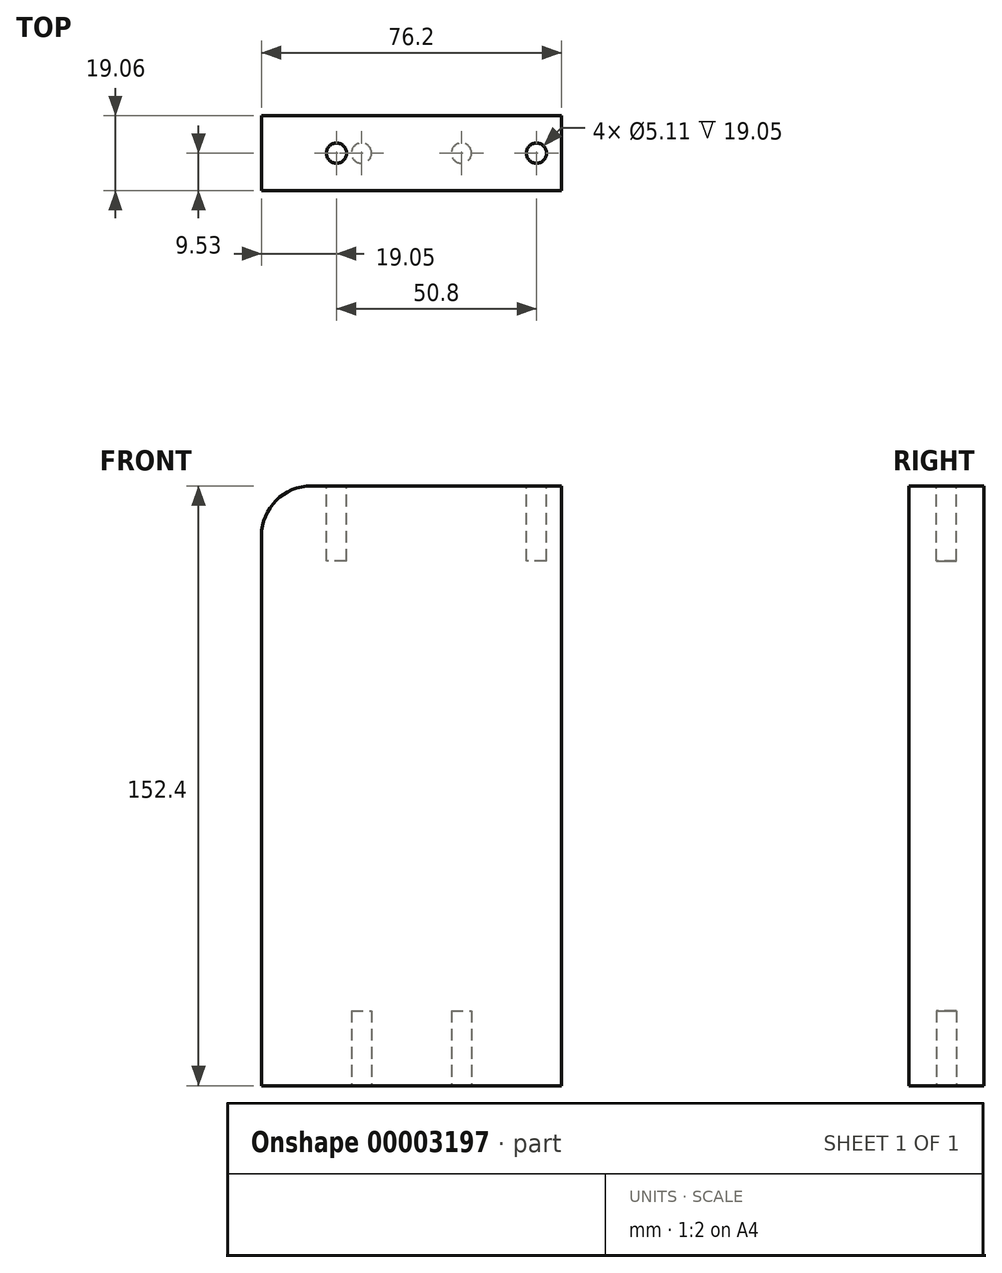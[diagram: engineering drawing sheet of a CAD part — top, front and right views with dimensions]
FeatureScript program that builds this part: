
annotation { "Feature Type Name" : "Feature", "Feature Type Description" : "" }
export const myFeature = defineFeature(function(context is Context, id is Id, definition is map)
    precondition{}
    {
        {
            var Q0;
            Q0=qCreatedBy(makeId("Front.planeOp"),FACE);
            var sketch = newSketch(context, id + "F0", { "sketchPlane" : qUnion([Q0])});
            skLineSegment(sketch, "E0", {"start": v(0, 0) * mm, "end": v(0, -152.4) * mm});
            skLineSegment(sketch, "E1", {"start": v(0, -152.4) * mm, "end": v(76.2, -152.4) * mm});
            skLineSegment(sketch, "E2", {"start": v(76.2, -152.4) * mm, "end": v(76.2, 0) * mm});
            skLineSegment(sketch, "E3", {"start": v(76.2, 0) * mm, "end": v(0, 0) * mm});
            skSolve(sketch);
        }
        {
            var Q0;
            Q0=makeQuery(id+"F0.imprint","IMPRINT",FACE,{"disambiguationData":[TD([[makeQuery(id+"F0.imprint","IMPRINT",EDGE,{"derivedFrom":sQuery(id+"F0.wireOp",EDGE,"E0")}),1.0]])]});
            extrude(context, id + "F1", {"entities" : qUnion([Q0]), "endBound" : BoundingType.SYMMETRIC, "depth" : 19.05 * mm});
        }
        {
            var Q0;
            Q0=makeQuery(id+"F1.opExtrude","SWEPT_FACE",FACE,{"disambiguationData":[OSD([sQuery(id+"F0.wireOp",EDGE,"E3")])]});
            var sketch = newSketch(context, id + "F2", { "sketchPlane" : qUnion([Q0])});
            skLineSegment(sketch, "E4", {"start": v(0, 0) * mm, "end": v(76.2, 0) * mm, "construction": true});
            skLineSegment(sketch, "E5", {"start": v(19.05, 9.53) * mm, "end": v(19.05, -9.53) * mm, "construction": true});
            skLineSegment(sketch, "E6", {"start": v(69.85, 9.53) * mm, "end": v(69.85, -9.53) * mm, "construction": true});
            skCircle(sketch, "E7", {"center": v(19.05, 0) * mm, "radius": 2.55 * mm});
            skCircle(sketch, "E8", {"center": v(69.85, 0) * mm, "radius": 2.55 * mm});
            skSolve(sketch);
        }
        {
            var Q0;
            Q0=makeQuery(id+"F2.imprint","IMPRINT",FACE,{"disambiguationData":[TD([[makeQuery(id+"F2.imprint","IMPRINT",EDGE,{"derivedFrom":sQuery(id+"F2.wireOp",EDGE,"E7")}),1.0]])]});
            var Q1;
            Q1=makeQuery(id+"F2.imprint","IMPRINT",FACE,{"disambiguationData":[TD([[makeQuery(id+"F2.imprint","IMPRINT",EDGE,{"derivedFrom":sQuery(id+"F2.wireOp",EDGE,"E8")}),1.0]])]});
            extrude(context, id + "F3", {"entities" : qUnion([Q0, Q1]), "operationType" : NewBodyOperationType.REMOVE, "oppositeDirection" : true, "depth" : 19.05 * mm});
        }
        {
            var Q0;
            Q0=makeQuery(id+"F1.opExtrude","SWEPT_FACE",FACE,{"disambiguationData":[OSD([sQuery(id+"F0.wireOp",EDGE,"E1")])]});
            var sketch = newSketch(context, id + "F4", { "sketchPlane" : qUnion([Q0])});
            skLineSegment(sketch, "E9", {"start": v(0, 0) * mm, "end": v(76.2, 0) * mm, "construction": true});
            skLineSegment(sketch, "E10", {"start": v(25.4, 9.53) * mm, "end": v(25.4, -9.53) * mm, "construction": true});
            skLineSegment(sketch, "E11", {"start": v(50.8, 9.53) * mm, "end": v(50.8, -9.53) * mm, "construction": true});
            skCircle(sketch, "E12", {"center": v(25.4, 0) * mm, "radius": 2.55 * mm});
            skCircle(sketch, "E13", {"center": v(50.8, 0) * mm, "radius": 2.55 * mm});
            skSolve(sketch);
        }
        {
            var Q0;
            Q0 = qSketchRegion(id + "F4", true);
            extrude(context, id + "F5", {"entities" : qUnion([Q0]), "operationType" : NewBodyOperationType.REMOVE, "oppositeDirection" : true, "depth" : 19.05 * mm});
        }
        {
            var Q0;
            Q0=makeQuery(id+"F1.opExtrude","SWEPT_EDGE",EDGE,{"disambiguationData":[OSD([sQuery(id+"F0.wireOp",EDGE,"E0"),sQuery(id+"F0.wireOp",EDGE,"E3")])]});
            fillet(context, id + "F6", {"entities" : qUnion([Q0]), "radius" : 12.7 * mm, "tangentPropagation" : true, "allowEdgeOverflow" : false});
        }
    });
